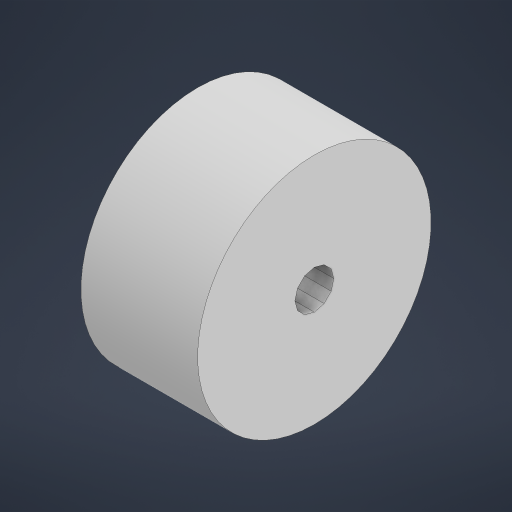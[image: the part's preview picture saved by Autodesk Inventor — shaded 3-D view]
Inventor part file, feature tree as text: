
AUTODESK INVENTOR PART (.ipt)
format: ipt  version: 2024 (Build 280153000, 153)  size: 175,104 bytes
history: native  units: mm
features: other x1, extrude x1, sketch x1
ambient origin geometry x8: Origin, YZ Plane, XZ Plane, XY Plane, X Axis, Y Axis, Z Axis, Center Point
bodies: Body1 (feature_tree)
feature tree (3):
  other  "솔리드1"
  extrude  "돌출1"  Depth=5.0mm
  sketch  "스케치1"
